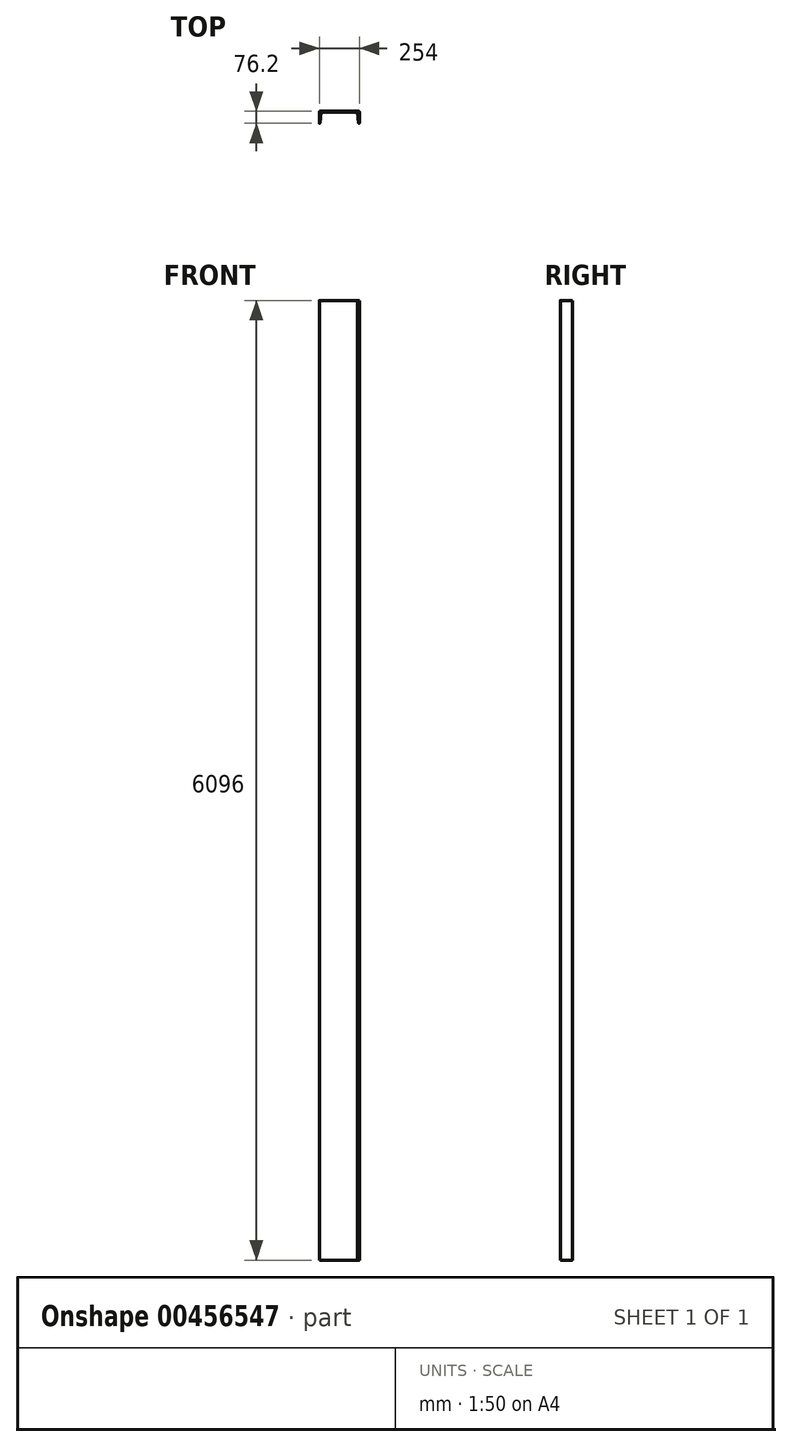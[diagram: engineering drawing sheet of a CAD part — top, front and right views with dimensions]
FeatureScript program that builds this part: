
annotation { "Feature Type Name" : "Feature", "Feature Type Description" : "" }
export const myFeature = defineFeature(function(context is Context, id is Id, definition is map)
    precondition{}
    {
        {
            var Q0;
            Q0=qCreatedBy(makeId("Top.planeOp"),FACE);
            var sketch = newSketch(context, id + "F0", { "sketchPlane" : qUnion([Q0])});
            skLineSegment(sketch, "E0", {"start": v(0, 0) * mm, "end": v(254, 0) * mm});
            skLineSegment(sketch, "E1", {"start": v(254, 0) * mm, "end": v(254, -76.2) * mm, "construction": true});
            skLineSegment(sketch, "E2", {"start": v(0, -76.2) * mm, "end": v(0, 0) * mm, "construction": true});
            skLineSegment(sketch, "E3", {"start": v(0, 0) * mm, "end": v(0, -4.76) * mm, "construction": true});
            skLineSegment(sketch, "E4", {"start": v(0, -4.76) * mm, "end": v(254, -4.76) * mm, "construction": true});
            skLineSegment(sketch, "E5", {"start": v(254, -76.2) * mm, "end": v(249.24, -76.2) * mm, "construction": true});
            skLineSegment(sketch, "E6", {"start": v(254, -4.76) * mm, "end": v(241.3, -4.76) * mm, "construction": true});
            skLineSegment(sketch, "E7", {"start": v(0, -4.76) * mm, "end": v(12.7, -4.76) * mm, "construction": true});
            skLineSegment(sketch, "E8", {"start": v(0, -76.2) * mm, "end": v(4.76, -76.2) * mm, "construction": true});
            skLineSegment(sketch, "E9", {"start": v(4.76, -76.2) * mm, "end": v(12.7, -4.76) * mm, "construction": true});
            skLineSegment(sketch, "E10", {"start": v(249.24, -76.2) * mm, "end": v(241.3, -4.76) * mm, "construction": true});
            skLineSegment(sketch, "E11", {"start": v(0, 0) * mm, "end": v(0, -76.2) * mm});
            skLineSegment(sketch, "E12", {"start": v(4.76, -76.2) * mm, "end": v(12.7, -4.76) * mm});
            skLineSegment(sketch, "E13", {"start": v(241.3, -4.76) * mm, "end": v(249.24, -76.2) * mm});
            skLineSegment(sketch, "E14", {"start": v(254, -76.2) * mm, "end": v(254, 0) * mm});
            skLineSegment(sketch, "E15", {"start": v(12.7, -4.76) * mm, "end": v(241.3, -4.76) * mm});
            skLineSegment(sketch, "E16", {"start": v(0, -76.2) * mm, "end": v(4.76, -76.2) * mm});
            skLineSegment(sketch, "E17", {"start": v(249.24, -76.2) * mm, "end": v(254, -76.2) * mm});
            skSolve(sketch);
        }
        {
            var Q0;
            Q0 = qSketchRegion(id + "F0", true);
            extrude(context, id + "F1", {"entities" : qUnion([Q0]), "depth" : 6096 * mm});
        }
        {
            var Q0;
            Q0=makeQuery(id+"F1.opExtrude","SWEPT_EDGE",EDGE,{"disambiguationData":[OSD([sQuery(id+"F0.wireOp",EDGE,"E11"),sQuery(id+"F0.wireOp",EDGE,"E16")])]});
            var Q1;
            Q1=makeQuery(id+"F1.opExtrude","SWEPT_EDGE",EDGE,{"disambiguationData":[OSD([sQuery(id+"F0.wireOp",EDGE,"E12"),sQuery(id+"F0.wireOp",EDGE,"E16")])]});
            var Q2;
            Q2=makeQuery(id+"F1.opExtrude","SWEPT_EDGE",EDGE,{"disambiguationData":[OSD([sQuery(id+"F0.wireOp",EDGE,"E12"),sQuery(id+"F0.wireOp",EDGE,"E15")])]});
            var Q3;
            Q3=makeQuery(id+"F1.opExtrude","SWEPT_EDGE",EDGE,{"disambiguationData":[OSD([sQuery(id+"F0.wireOp",EDGE,"E13"),sQuery(id+"F0.wireOp",EDGE,"E17")])]});
            var Q4;
            Q4=makeQuery(id+"F1.opExtrude","SWEPT_EDGE",EDGE,{"disambiguationData":[OSD([sQuery(id+"F0.wireOp",EDGE,"E14"),sQuery(id+"F0.wireOp",EDGE,"E17")])]});
            var Q5;
            Q5=makeQuery(id+"F1.opExtrude","SWEPT_EDGE",EDGE,{"disambiguationData":[OSD([sQuery(id+"F0.wireOp",EDGE,"E0"),sQuery(id+"F0.wireOp",EDGE,"E14")])]});
            fillet(context, id + "F2", {"entities" : qUnion([Q0, Q1, Q2, Q3, Q4, Q5]), "radius" : 1.27 * mm, "tangentPropagation" : true, "allowEdgeOverflow" : false});
        }
        {
            var Q0;
            Q0=makeQuery(id+"F1.opExtrude","SWEPT_EDGE",EDGE,{"disambiguationData":[OSD([sQuery(id+"F0.wireOp",EDGE,"E0"),sQuery(id+"F0.wireOp",EDGE,"E11")])]});
            fillet(context, id + "F3", {"entities" : qUnion([Q0]), "radius" : 3.17 * mm, "tangentPropagation" : true, "allowEdgeOverflow" : false});
        }
    });
